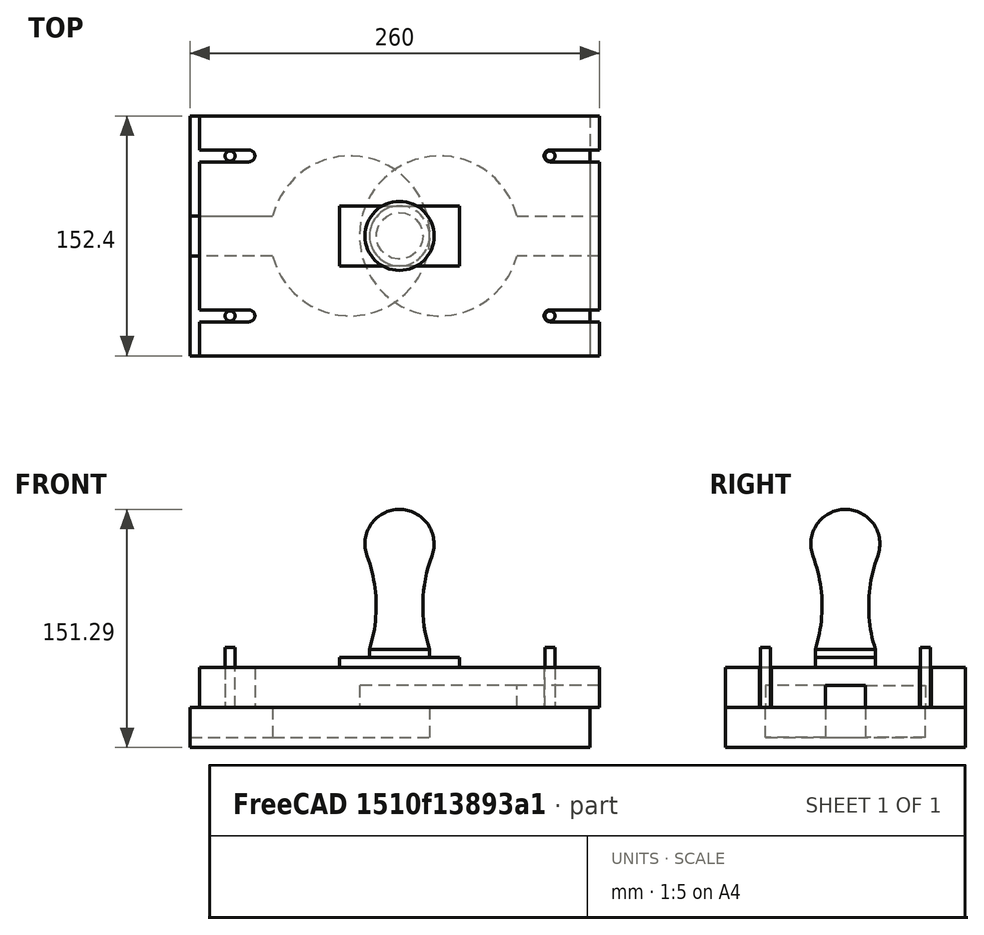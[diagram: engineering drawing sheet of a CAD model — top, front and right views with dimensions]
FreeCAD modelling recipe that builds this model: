
FCSTD DOCUMENT  (FreeCAD 0.17R13541 (Git))
Label: bell-metaldetector-FEM
License: All rights reserved
LicenseURL: http://en.wikipedia.org/wiki/All_rights_reserved
objects: Sketcher::SketchObject×8, PartDesign::Pad×4, PartDesign::Mirrored×4, PartDesign::Pocket×3, PartDesign::Body×3, Fem::FemSolverObjectPython×3, Fem::FemMeshObjectPython×3, PartDesign::MultiTransform×2, PartDesign::ShapeBinder×2, Fem::ConstraintFixed×2, Fem::ConstraintForce×2, App::MaterialObjectPython×2, Fem::FemAnalysis×2, PartDesign::Revolution×1, Part::Fuse×1, Fem::FemResultObjectPython×1
note: 36 computed .brp shape members not serialized (recipe doc carries the construction recipe); baked Part::Feature solids carry a one-line shape summary decoded from their .brp

FEATURE [Sketcher::SketchObject] Sketch
  MapMode = 5
  Support = -> [XY_Plane]
  sketch-geometry (4):
    g0: LineSegment StartX=-127 StartY=76.2 StartZ=0 EndX=127 EndY=76.2 EndZ=0
    g1: LineSegment StartX=127 StartY=76.2 StartZ=0 EndX=127 EndY=-76.2 EndZ=0
    g2: LineSegment StartX=127 StartY=-76.2 StartZ=0 EndX=-127 EndY=-76.2 EndZ=0
    g3: LineSegment StartX=-127 StartY=-76.2 StartZ=0 EndX=-127 EndY=76.2 EndZ=0
  constraints (11):
    c: Coincident(g0,g1)
    c: Coincident(g1,g2)
    c: Coincident(g2,g3)
    c: Coincident(g3,g0)
    c: Horizontal(g0)
    c: Horizontal(g2)
    c: Vertical(g1)
    c: Vertical(g3)
    c: DistanceX(g0,g0) = 254
    c: DistanceY(g1,g1) = 152.4
    c: Symmetric(g2,g0,g-1)
FEATURE [PartDesign::Pad] Pad
  Length = 25.4
  Length2 = 100
  Profile = -> Sketch
  Type = 0
FEATURE [Sketcher::SketchObject] Sketch001
  MapMode = 5
  Placement = pos=(0,0,25.4) rot=(0,0,1;0rad)
  Support = -> [Pad]
  sketch-geometry (1):
    g0: Circle CenterX=-101.6 CenterY=50.8 CenterZ=0 NormalX=0 NormalY=0 NormalZ=1 AngleXU=0 Radius=3.175
  constraints (3):
    c: DistanceX(g0) = -101.6
    c: Radius(g0) = 3.175
    c: DistanceY(g0) = 50.8
FEATURE [PartDesign::Pad] Pad001
  BaseFeature = -> Pad
  Length = 38.1
  Length2 = 100
  Profile = -> Sketch001
  Type = 0
FEATURE [PartDesign::Mirrored] Mirrored
  MirrorPlane = -> XZ_Plane
FEATURE [PartDesign::Mirrored] Mirrored001
  MirrorPlane = -> Sketch001 [V_Axis]
FEATURE [PartDesign::MultiTransform] MultiTransform
  BaseFeature = -> Pad001
  Originals = -> [Pad001]
  Transformations = -> [Mirrored,Mirrored001]
FEATURE [Sketcher::SketchObject] Sketch002
  ExternalGeometry = -> [MultiTransform]
  MapMode = 5
  Placement = pos=(0,0,25.4) rot=(0,0,1;0rad)
  Support = -> [MultiTransform]
  sketch-geometry (4):
    g0: ArcOfCircle CenterX=-25.4 CenterY=0 CenterZ=0 NormalX=0 NormalY=0 NormalZ=1 AngleXU=0 Radius=50.8 StartAngle=3.39427 EndAngle=9.1721
    g1: LineSegment StartX=-127 StartY=12.7 StartZ=0 EndX=-74.5869 EndY=12.7 EndZ=0
    g2: LineSegment StartX=-74.5869 StartY=-12.7 StartZ=0 EndX=-127 EndY=-12.7 EndZ=0
    g3: LineSegment StartX=-127 StartY=-12.7 StartZ=0 EndX=-127 EndY=12.7 EndZ=0
  constraints (13):
    c: PointOnObject(g0,g-1)
    c: Radius(g0) = 50.8
    c: Coincident(g2,g3)
    c: Coincident(g3,g1)
    c: Horizontal(g1)
    c: Horizontal(g2)
    c: Vertical(g3)
    c: Coincident(g0,g1)
    c: Symmetric(g1,g2,g-1)
    c: DistanceX(g0) = -25.4
    c: DistanceY(g3,g3) = 25.4
    c: Coincident(g2,g0)
    c: PointOnObject(g1,g-3)
FEATURE [PartDesign::Pocket] Pocket
  BaseFeature = -> MultiTransform
  Length = 19.05
  Length2 = 100
  Profile = -> Sketch002
  Type = 0
FEATURE [PartDesign::Body] Body  label="Bottom Block"
  Group = -> [Sketch,Pad,Sketch001,Pad001,MultiTransform,Mirrored,Mirrored001,Sketch002,Pocket]
  Origin = -> Origin
  Placement = pos=(-6,0,0) rot=(0,0,1;0rad)
  Tip = -> Pocket
FEATURE [PartDesign::ShapeBinder] ShapeBinder
  Support = -> [Pocket]
FEATURE [Sketcher::SketchObject] Sketch003
  ExternalGeometry = -> [ShapeBinder]
  MapMode = 5
  Placement = pos=(0,0,25.4) rot=(0,0,1;0rad)
  Support = -> [ShapeBinder]
  sketch-geometry (4):
    g0: LineSegment StartX=-127 StartY=76.2 StartZ=0 EndX=127 EndY=76.2 EndZ=0
    g1: LineSegment StartX=127 StartY=76.2 StartZ=0 EndX=127 EndY=-76.2 EndZ=0
    g2: LineSegment StartX=127 StartY=-76.2 StartZ=0 EndX=-127 EndY=-76.2 EndZ=0
    g3: LineSegment StartX=-127 StartY=-76.2 StartZ=0 EndX=-127 EndY=76.2 EndZ=0
  constraints (10):
    c: Coincident(g0,g1)
    c: Coincident(g1,g2)
    c: Coincident(g2,g3)
    c: Coincident(g3,g0)
    c: Horizontal(g0)
    c: Horizontal(g2)
    c: Vertical(g1)
    c: Vertical(g3)
    c: Coincident(g0,g-3)
    c: Coincident(g1,g-4)
FEATURE [PartDesign::Pad] Pad002
  Length = 25.5
  Length2 = 100
  Profile = -> Sketch003
  Type = 0
FEATURE [Sketcher::SketchObject] Sketch004
  ExternalGeometry = -> [ShapeBinder]
  MapMode = 5
  Placement = pos=(0,0,25.4) rot=(0,0,1;0rad)
  Support = -> [ShapeBinder]
  sketch-geometry (5):
    g0: LineSegment StartX=-127 StartY=54.55 StartZ=0 EndX=-95.6 EndY=54.55 EndZ=0
    g1: LineSegment StartX=-95.6 StartY=47.05 StartZ=0 EndX=-127 EndY=47.05 EndZ=0
    g2: LineSegment StartX=-127 StartY=47.05 StartZ=0 EndX=-127 EndY=54.55 EndZ=0
    g3: ArcOfCircle CenterX=-95.6 CenterY=50.8 CenterZ=0 NormalX=0 NormalY=0 NormalZ=1 AngleXU=0 Radius=3.75 StartAngle=4.71239 EndAngle=7.85398
    g4: LineSegment [constr] StartX=-101.6 StartY=50.8 StartZ=0 EndX=-95.6 EndY=50.8 EndZ=0
  constraints (13):
    c: Coincident(g1,g2)
    c: Coincident(g2,g0)
    c: Horizontal(g0)
    c: Horizontal(g1)
    c: Vertical(g2)
    c: PointOnObject(g0,g-4)
    c: Radius(g3) = 3.75
    c: Tangent(g3,g0) = 1.5708
    c: Tangent(g3,g1) = 1.5708
    c: Coincident(g4,g-3)
    c: Coincident(g4,g3)
    c: DistanceX(g4,g4) = 6
    c: Horizontal(g4)
FEATURE [PartDesign::Pocket] Pocket001
  BaseFeature = -> Pad002
  Length = 5
  Length2 = 100
  Profile = -> Sketch004
  Reversed = true
  Type = 1
FEATURE [PartDesign::Mirrored] Mirrored002
  MirrorPlane = -> YZ_Plane001
FEATURE [PartDesign::Mirrored] Mirrored003
  MirrorPlane = -> XZ_Plane001
FEATURE [PartDesign::MultiTransform] MultiTransform001
  BaseFeature = -> Pocket001
  Originals = -> [Pocket001]
  Transformations = -> [Mirrored002,Mirrored003]
FEATURE [Sketcher::SketchObject] Sketch005
  ExternalGeometry = -> [ShapeBinder]
  MapMode = 5
  Placement = pos=(0,0,25.4) rot=(0,0,1;0rad)
  Support = -> [ShapeBinder]
  sketch-geometry (5):
    g0: ArcOfCircle CenterX=25.4 CenterY=0 CenterZ=0 NormalX=0 NormalY=0 NormalZ=1 AngleXU=0 Radius=50.8 StartAngle=0.25268 EndAngle=6.03051
    g1: LineSegment StartX=74.5869 StartY=12.7 StartZ=0 EndX=127 EndY=12.7 EndZ=0
    g2: LineSegment StartX=127 StartY=12.7 StartZ=0 EndX=127 EndY=-12.7 EndZ=0
    g3: LineSegment StartX=127 StartY=-12.7 StartZ=0 EndX=74.5869 EndY=-12.7 EndZ=0
    g4: LineSegment [constr] StartX=-74.5869 StartY=12.7 StartZ=0 EndX=-74.5869 EndY=-12.7 EndZ=0
  constraints (16):
    c: PointOnObject(g0,g-1)
    c: Equal(g0,g-3)
    c: Symmetric(g0,g-3,g-2)
    c: Coincident(g1,g2)
    c: Coincident(g2,g3)
    c: Horizontal(g1)
    c: Horizontal(g3)
    c: Vertical(g2)
    c: PointOnObject(g2,g-4)
    c: Coincident(g0,g1)
    c: Coincident(g0,g3)
    c: Coincident(g3,g0)
    c: Symmetric(g1,g2,g-1)
    c: Coincident(g4,g-3)
    c: Coincident(g4,g-3)
    c: Equal(g2,g4)
FEATURE [PartDesign::Pocket] Pocket002
  BaseFeature = -> MultiTransform001
  Length = 14
  Length2 = 100
  Profile = -> Sketch005
  Reversed = true
  Type = 0
FEATURE [PartDesign::Body] Body001  label="Top Block"
  Group = -> [ShapeBinder,Sketch003,Pad002,Sketch004,Pocket001,MultiTransform001,Mirrored002,Mirrored003,Sketch005,Pocket002]
  Origin = -> Origin001
  Tip = -> Pocket002
FEATURE [PartDesign::ShapeBinder] ShapeBinder001
  Support = -> [Pocket002]
FEATURE [Sketcher::SketchObject] Sketch006
  MapMode = 5
  Placement = pos=(0,0,50.9) rot=(0,0,1;0rad)
  Support = -> [ShapeBinder001]
  sketch-geometry (4):
    g0: LineSegment StartX=-38.1 StartY=19.05 StartZ=0 EndX=38.1 EndY=19.05 EndZ=0
    g1: LineSegment StartX=38.1 StartY=19.05 StartZ=0 EndX=38.1 EndY=-19.05 EndZ=0
    g2: LineSegment StartX=38.1 StartY=-19.05 StartZ=0 EndX=-38.1 EndY=-19.05 EndZ=0
    g3: LineSegment StartX=-38.1 StartY=-19.05 StartZ=0 EndX=-38.1 EndY=19.05 EndZ=0
  constraints (11):
    c: Coincident(g0,g1)
    c: Coincident(g1,g2)
    c: Coincident(g2,g3)
    c: Coincident(g3,g0)
    c: Horizontal(g0)
    c: Horizontal(g2)
    c: Vertical(g1)
    c: Vertical(g3)
    c: Symmetric(g0,g2,g-1)
    c: DistanceX(g0,g0) = 76.2
    c: DistanceY(g1,g1) = 38.1
FEATURE [PartDesign::Pad] Pad003
  Length = 6.35
  Length2 = 100
  Profile = -> Sketch006
  Type = 0
FEATURE [Sketcher::SketchObject] Sketch007
  ExternalGeometry = -> [Pad003]
  MapMode = 5
  Placement = pos=(0,0,0) rot=(1,0,0;1.5708rad)
  Support = -> [XZ_Plane002]
  sketch-geometry (5):
    g0: ArcOfCircle CenterX=0 CenterY=129.37 CenterZ=0 NormalX=0 NormalY=0 NormalZ=1 AngleXU=0 Radius=21.92 StartAngle=5.92846 EndAngle=7.85398
    g1: ArcOfCircle CenterX=106.828 CenterY=89.8018 CenterZ=0 NormalX=0 NormalY=0 NormalZ=1 AngleXU=0 Radius=92 StartAngle=2.78687 EndAngle=3.44574
    g2: LineSegment StartX=19.05 StartY=62.25 StartZ=0 EndX=19.05 EndY=57.25 EndZ=0
    g3: LineSegment StartX=19.05 StartY=57.25 StartZ=0 EndX=1.1e-11 EndY=57.25 EndZ=0
    g4: LineSegment StartX=1.1e-11 StartY=57.25 StartZ=0 EndX=1.1e-11 EndY=151.29 EndZ=0
  constraints (16):
    c: PointOnObject(g0,g-2)
    c: Tangent(g1,g0) = 1.5708
    c: PointOnObject(g0,g-2)
    c: Coincident(g2,g1)
    c: PointOnObject(g2,g-3)
    c: Vertical(g2)
    c: Coincident(g2,g3)
    c: Coincident(g3,g4)
    c: Vertical(g4)
    c: Coincident(g0,g4)
    c: DistanceY(g2,g2) = 5
    c: Horizontal(g3)
    c: DistanceY(g4,g4) = 94.04
    c: DistanceX(g3,g3) = 19.05
    c: Radius(g1) = 92
    c: DistanceY(g3,g0) = 72.12
FEATURE [PartDesign::Revolution] Revolution
  Angle = 360
  Axis = (0,0,1)
  Base = (0,0,0)
  BaseFeature = -> Pad003
  Profile = -> Sketch007
  ReferenceAxis = -> Z_Axis002
  Reversed = true
FEATURE [PartDesign::Body] Body002  label="Handle"
  Group = -> [ShapeBinder001,Sketch006,Pad003,Sketch007,Revolution]
  Origin = -> Origin002
  Tip = -> Revolution
FEATURE [Part::Fuse] Fusion
  Base = -> Body001
  Tool = -> Body002
FEATURE [Fem::FemSolverObjectPython] CalculiXccxTools  # FEM object (typed FeaturePython)
  AnalysisType = 0
  BeamShellResultOutput3D = false
  EigenmodeHighLimit = 1000000
  EigenmodeLowLimit = 0
  EigenmodesCount = 10
  GeometricalNonlinearity = 0
  IterationsControlParameterCutb = 0.25,0.5,0.75,0.85,,,1.5,
  IterationsControlParameterIter = 4,8,9,200,10,400,,200,,
  IterationsControlParameterTimeUse = false
  IterationsThermoMechMaximum = 200
  IterationsUserDefinedIncrementations = false
  IterationsUserDefinedTimeStepLength = false
  MaterialNonlinearity = 0
  MatrixSolverType = 0
  SplitInputWriter = false
  ThermoMechSteadyState = true
  TimeEnd = 1
  TimeInitialStep = 1
FEATURE [Fem::FemMeshObjectPython] FEMMeshGmsh  # FEM object (typed FeaturePython)
  Algorithm2D = 0
  Algorithm3D = 0
  CharacteristicLengthMax = 0
  CharacteristicLengthMin = 0
  CoherenceMesh = true
  ElementDimension = 0
  ElementOrder = 1
  GeometryTolerance = 1e-06
  GroupsOfNodes = false
  HighOrderOptimize = false
  OptimizeNetgen = false
  OptimizeStd = true
  Part = -> Fusion
  RecombineAll = false
FEATURE [Fem::ConstraintFixed] FemConstraintFixed
  NormalDirection = (0,0,-1)
  Normals = (14) [(0,0,-1),(0,0,-1),(0,0,-1),(0,0,-1),(0,0,-1),(0,0,-1),(0,0,-1),(0,0,-1),(0,0,-1),(0,0,-1),(0,0,-1),(0,0,-1),(0,0,-1),(0,0,-1)]
  Points = (14) [(127,-76.2,25.4),(42.3333,-76.2,25.4),(-42.3333,-76.2,25.4),(-127,-76.2,25.4),(127,-25.4,25.4),(-42.3333,-25.4,25.4),(-127,-25.4,25.4),+7 more]
  References = -> [Fusion]
  Scale = 15
FEATURE [Fem::ConstraintForce] FemConstraintForce
  Direction = -> Fusion [Face20]
  DirectionVector = (1,0,0)
  Force = 9000
  NormalDirection = (-0.820772,2e-12,0.571256)
  Points = (44) [(20.5553,-6.84881e-11,121.756),(-10.2777,-17.8014,121.756),(-10.2777,17.8014,121.756),(20.5553,-6.84831e-11,121.756),(21.0227,-6.65809e-11,135.577),+39 more]
  References = -> [Fusion]
  Scale = 7
FEATURE [App::MaterialObjectPython] SolidMaterial  # material (typed FeaturePython)
  Category = 0
  Material = Density=700.0 kg/m^3,Description=A standard construction wood,Father=Aggregate,Name=Wood,PoissonRatio=0.05,+5 more (map truncated)
FEATURE [Fem::FemSolverObjectPython] CalculiXccxTools001  # FEM object (typed FeaturePython)
  AnalysisType = 0
  BeamShellResultOutput3D = false
  EigenmodeHighLimit = 1000000
  EigenmodeLowLimit = 0
  EigenmodesCount = 10
  GeometricalNonlinearity = 0
  IterationsControlParameterCutb = 0.25,0.5,0.75,0.85,,,1.5,
  IterationsControlParameterIter = 4,8,9,200,10,400,,200,,
  IterationsControlParameterTimeUse = false
  IterationsThermoMechMaximum = 200
  IterationsUserDefinedIncrementations = false
  IterationsUserDefinedTimeStepLength = false
  MaterialNonlinearity = 0
  MatrixSolverType = 0
  SplitInputWriter = false
  ThermoMechSteadyState = true
  TimeEnd = 1
  TimeInitialStep = 1
FEATURE [Fem::FemMeshObjectPython] Result_mesh  # FEM object (typed FeaturePython)
FEATURE [Fem::FemResultObjectPython] CalculiX_static_results  # FEM object (typed FeaturePython)
  DisplacementLengths = [0,8.1403e-05,0,4.09998e-05,0,5.47332e-05,0,7.1095e-05,0,0,0,0,0,0,0,0,0,0,0,0,0,0,0,0,0,0,0,0,0.000118487,0.000201965,0.000161582,0.000161575,0.000285996,0.000200135,0.000426076,0.000119691,0.000275486,5.56487e-05,0.000289169,8.18043e-05,+2838 more]
  DisplacementVectors = (2878) [(0,0,0),(6.64685e-05,-2.74203e-05,3.81642e-05),(0,0,0),(-5.82511e-06,-3.63502e-05,1.80476e-05),(0,0,0),(4.66126e-05,-2.74275e-05,8.40954e-06),(0,0,0),+2871 more]
  Eigenmode = 0
  EigenmodeFrequency = 0
  MaxShear = [0.0272864,0.00253766,0.0200174,0.0065484,0.00969071,0.00716712,0.0194921,0.0291469,0.0489875,0.0881967,0.049282,0.0490527,0.0801425,0.0508196,0.00975891,0.0274009,0.0176709,0.0196986,0.0704934,0.247394,0.0777387,0.0415483,2.76646,3.24839,+2854 more]
  Mesh = -> Result_mesh
  NodeNumbers = [1,2,3,4,5,6,7,8,9,10,11,12,13,14,15,16,17,18,19,20,21,22,23,24,25,26,27,28,29,30,31,32,33,34,35,36,37,38,39,40,41,42,43,44,45,46,47,48,49,50,51,52,53,54,55,56,57,58,59,60,61,62,63,64,65,66,67,68,69,+2809 more]
  PrincipalMax = [0.0497783,0.00071804,0.0312318,0.00366602,0.0156678,0.00382675,0.00254363,0.0161813,0.0550425,0.113944,0.0897616,0.0894468,0.107351,0.062652,0.0157387,0.050026,0.0263435,0.00290872,0.0810773,0.26311,0.00972118,0.0316626,1.92804,1.39034,+2854 more]
  PrincipalMed = [0.00151766,-0.00325236,0.00107366,-0.00394606,-0.000899496,-0.00610573,0.000479628,-0.0215486,0.00248314,0.00409552,0.00354916,0.00355231,0.00250758,0.00396689,-0.000898124,0.00152832,0.000762903,0.000621006,0.00233571,-0.0052862,+2858 more]
  PrincipalMin = [-0.00479456,-0.00435727,-0.00880292,-0.00943078,-0.00371362,-0.0105075,-0.0364406,-0.0421124,-0.0429324,-0.0624498,-0.00880237,-0.00865865,-0.0529343,-0.0389872,-0.00377914,-0.00477582,-0.00899834,-0.0364885,-0.0599095,-0.231678,-0.145756,+2857 more]
  ResultType = Fem::FemResultMechanical
  Stats = [-0.0399997,0.0429549,2.30027,-0.0318697,6.06373e-05,0.0313779,-0.706866,-0.0174147,0.49269,0,0.0589902,2.30214,0.00154737,4.966,127.527,-13.2978,2.48035,131.841,-50.0075,-0.296376,50.0924,-112.796,-3.00047,5.19278,0.000862354,2.74041,+13 more]
  StrainVectors = (2878) [(-8.97783e-08,-7.33413e-08,3.65072e-06),(-2.70297e-07,-4.56798e-08,-2.00893e-07),(6.68585e-09,-8.17065e-08,1.83771e-06),+2875 more]
  StressValues = [0.0517065,0.00462297,0.0361237,0.0113919,0.0181388,0.0127181,0.0379943,0.0512083,0.0849239,0.154288,0.0930054,0.0926057,0.140991,0.0883728,0.0182487,0.0519375,0.0316124,0.0383047,0.122376,0.429013,0.147172,0.0747489,4.914,5.9373,0.0742307,+2853 more]
  StressVectors = (2878) [(0.00118831,0.00137616,0.0439369),(-0.00341728,-0.000850226,-0.00262409),(0.00119558,0.000185382,0.0221216),(-0.00426966,0.000211717,-0.00565288),+2874 more]
  Time = 0
FEATURE [Fem::FemAnalysis] Analysis
  Group = -> [CalculiXccxTools,FEMMeshGmsh,FemConstraintFixed,FemConstraintForce,SolidMaterial,CalculiXccxTools001,CalculiX_static_results]
FEATURE [Fem::FemSolverObjectPython] CalculiXccxTools002  # FEM object (typed FeaturePython)
  AnalysisType = 0
  BeamShellResultOutput3D = false
  EigenmodeHighLimit = 1000000
  EigenmodeLowLimit = 0
  EigenmodesCount = 10
  GeometricalNonlinearity = 0
  IterationsControlParameterCutb = 0.25,0.5,0.75,0.85,,,1.5,
  IterationsControlParameterIter = 4,8,9,200,10,400,,200,,
  IterationsControlParameterTimeUse = false
  IterationsThermoMechMaximum = 2000
  IterationsUserDefinedIncrementations = false
  IterationsUserDefinedTimeStepLength = false
  MaterialNonlinearity = 0
  MatrixSolverType = 0
  SplitInputWriter = false
  ThermoMechSteadyState = true
  TimeEnd = 1
  TimeInitialStep = 0.01
FEATURE [Fem::FemMeshObjectPython] FEMMeshGmsh001  # FEM object (typed FeaturePython)
  Algorithm2D = 0
  Algorithm3D = 0
  CharacteristicLengthMax = 0
  CharacteristicLengthMin = 0
  CoherenceMesh = true
  ElementDimension = 0
  ElementOrder = 1
  GeometryTolerance = 1e-06
  GroupsOfNodes = false
  HighOrderOptimize = false
  OptimizeNetgen = false
  OptimizeStd = true
  Part = -> Fusion
  RecombineAll = false
FEATURE [Fem::ConstraintFixed] FemConstraintFixed001
  NormalDirection = (0,0,-1)
  Normals = (14) [(0,0,-1),(0,0,-1),(0,0,-1),(0,0,-1),(0,0,-1),(0,0,-1),(0,0,-1),(0,0,-1),(0,0,-1),(0,0,-1),(0,0,-1),(0,0,-1),(0,0,-1),(0,0,-1)]
  Points = (14) [(127,-76.2,25.4),(42.3333,-76.2,25.4),(-42.3333,-76.2,25.4),(-127,-76.2,25.4),(127,-25.4,25.4),(-42.3333,-25.4,25.4),(-127,-25.4,25.4),+7 more]
  References = -> [Fusion]
  Scale = 15
FEATURE [Fem::ConstraintForce] FemConstraintForce001
  DirectionVector = (1,0,0)
  Force = 9000
  NormalDirection = (-1,0,0)
  Points = (56) [(-38.1,-19.05,57.25),(-38.1,-6.35,57.25),(-38.1,6.35,57.25),(-38.1,19.05,57.25),(-38.1,-19.05,54.075),(-38.1,-6.35,54.075),(-38.1,6.35,54.075),+49 more]
  References = -> [Fusion]
  Reversed = true
  Scale = 6
FEATURE [App::MaterialObjectPython] SolidMaterial001  # material (typed FeaturePython)
  Category = 0
  Material = Density=700.0 kg/m^3,Description=A standard construction wood,Father=Aggregate,Name=Wood,PoissonRatio=0.05,+5 more (map truncated)
FEATURE [Fem::FemAnalysis] Analysis001
  Group = -> [CalculiXccxTools002,FEMMeshGmsh001,FemConstraintFixed001,FemConstraintForce001,SolidMaterial001]
